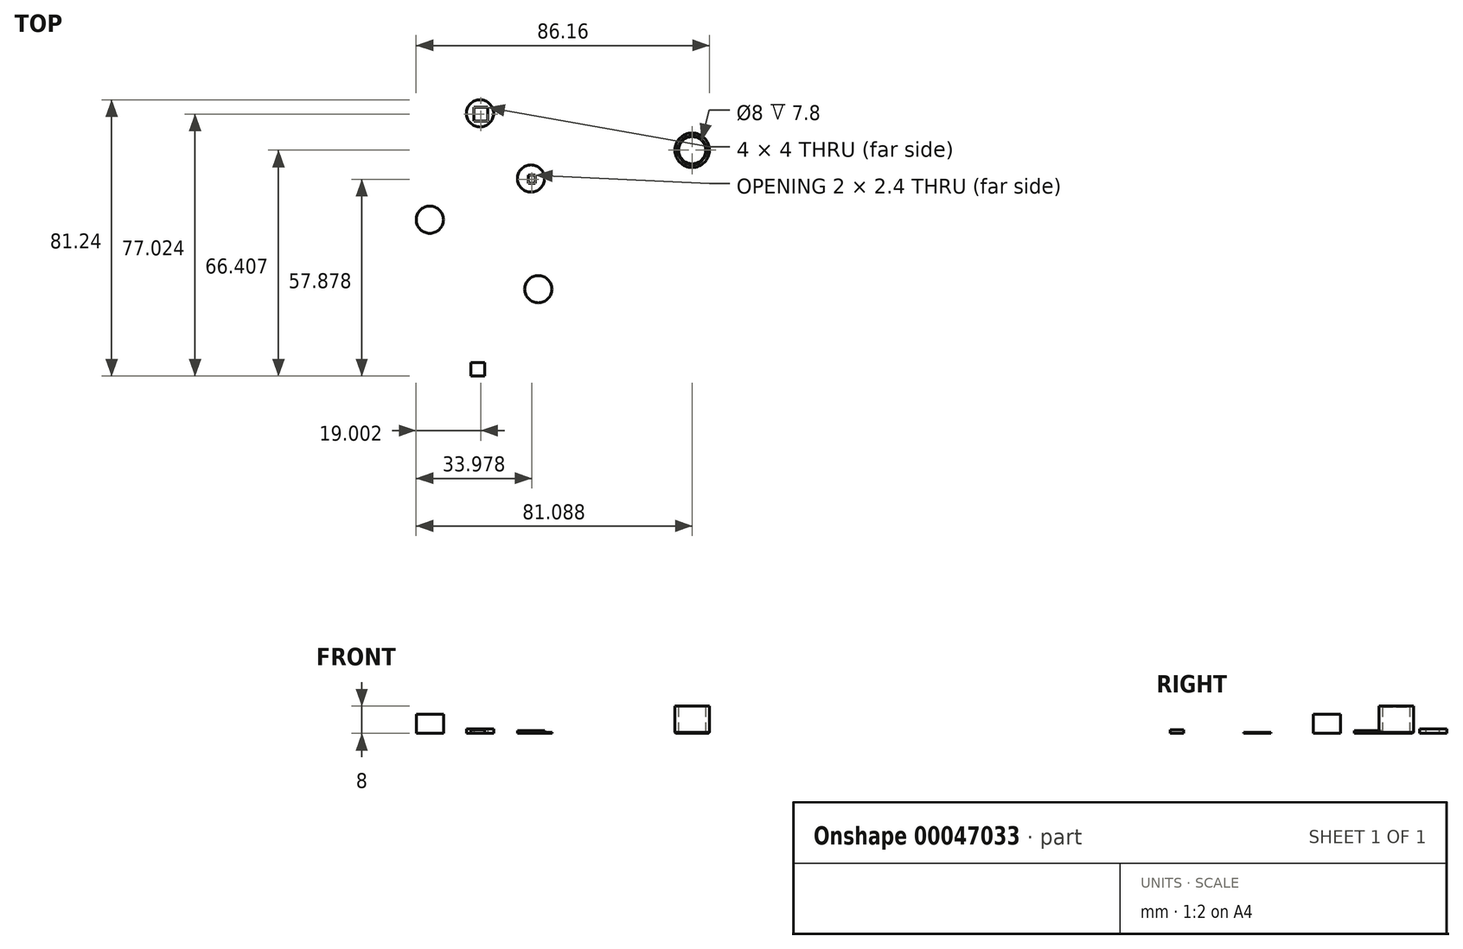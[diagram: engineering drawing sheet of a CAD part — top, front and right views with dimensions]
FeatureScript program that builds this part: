
annotation { "Feature Type Name" : "Feature", "Feature Type Description" : "" }
export const myFeature = defineFeature(function(context is Context, id is Id, definition is map)
    precondition{}
    {
        {
            var Q0;
            Q0=qCreatedBy(makeId("Top.planeOp"),FACE);
            var sketch = newSketch(context, id + "F0", { "sketchPlane" : qUnion([Q0])});
            skLineSegment(sketch, "E0.bottom", {"start": v(-30.94, 27.88) * mm, "end": v(-28.94, 27.88) * mm});
            skLineSegment(sketch, "E0.top", {"start": v(-30.94, 25.48) * mm, "end": v(-28.94, 25.48) * mm});
            skLineSegment(sketch, "E0.left", {"start": v(-30.94, 27.88) * mm, "end": v(-30.94, 25.48) * mm});
            skLineSegment(sketch, "E0.right", {"start": v(-28.94, 27.88) * mm, "end": v(-28.94, 25.48) * mm});
            skLineSegment(sketch, "E1", {"start": v(-28.94, 25.48) * mm, "end": v(-26.99, 25.48) * mm, "construction": true});
            skLineSegment(sketch, "E2", {"start": v(-26.99, 25.48) * mm, "end": v(-26.99, 23.28) * mm, "construction": true});
            skLineSegment(sketch, "E3", {"start": v(-28.94, 27.88) * mm, "end": v(-26.38, 27.88) * mm, "construction": true});
            skLineSegment(sketch, "E4", {"start": v(-26.38, 27.88) * mm, "end": v(-26.38, 29.87) * mm, "construction": true});
            skLineSegment(sketch, "E5", {"start": v(-30.94, 25.48) * mm, "end": v(-32.43, 25.48) * mm, "construction": true});
            skLineSegment(sketch, "E6", {"start": v(-32.43, 25.48) * mm, "end": v(-32.43, 22.62) * mm, "construction": true});
            skCircle(sketch, "E7", {"center": v(-30.19, 26.9) * mm, "radius": 4.83 * mm, "construction": true});
            skCircle(sketch, "E8", {"center": v(-30.19, 26.9) * mm, "radius": 4 * mm});
            skLineSegment(sketch, "E9", {"start": v(-30.56, 27.5) * mm, "end": v(-31.15, 27.5) * mm});
            skLineSegment(sketch, "E10", {"start": v(-30.56, 27.37) * mm, "end": v(-30.56, 28.22) * mm});
            skArc(sketch, "E11", {"start": v(-30.56, 27.88) * mm, "mid": v(-30.83, 27.77) * mm, "end": v(-30.94, 27.5) * mm});
            skSolve(sketch);
        }
        {
            var Q0;
            Q0=makeQuery(id+"F0.imprint","IMPRINT",FACE,{"disambiguationData":[TD([[makeQuery(id+"F0.imprint","IMPRINT",EDGE,{"derivedFrom":sQuery(id+"F0.wireOp",EDGE,"E8")}),1.0]])]});
            extrude(context, id + "F1", {"entities" : qUnion([Q0]), "depth" : 0.79 * mm});
        }
        {
            var Q0;
            Q0=qCreatedBy(makeId("Top.planeOp"),FACE);
            var sketch = newSketch(context, id + "F2", { "sketchPlane" : qUnion([Q0])});
            skLineSegment(sketch, "E12", {"start": v(-43.92, 44.62) * mm, "end": v(-41.97, 44.62) * mm, "construction": true});
            skLineSegment(sketch, "E13", {"start": v(-41.97, 44.62) * mm, "end": v(-41.97, 42.43) * mm, "construction": true});
            skLineSegment(sketch, "E14", {"start": v(-43.92, 47.02) * mm, "end": v(-41.36, 47.02) * mm, "construction": true});
            skLineSegment(sketch, "E15.right", {"start": v(-43.92, 47.02) * mm, "end": v(-43.92, 44.62) * mm, "construction": true});
            skLineSegment(sketch, "E15.left", {"start": v(-45.92, 47.02) * mm, "end": v(-45.92, 44.62) * mm, "construction": true});
            skLineSegment(sketch, "E16", {"start": v(-41.36, 47.02) * mm, "end": v(-41.36, 49.01) * mm, "construction": true});
            skLineSegment(sketch, "E15.top", {"start": v(-45.92, 44.62) * mm, "end": v(-43.92, 44.62) * mm, "construction": true});
            skLineSegment(sketch, "E17", {"start": v(-45.92, 44.62) * mm, "end": v(-47.4, 44.62) * mm, "construction": true});
            skLineSegment(sketch, "E15.bottom", {"start": v(-45.92, 47.02) * mm, "end": v(-43.92, 47.02) * mm, "construction": true});
            skLineSegment(sketch, "E18", {"start": v(-47.4, 44.62) * mm, "end": v(-47.4, 41.77) * mm, "construction": true});
            skCircle(sketch, "E19", {"center": v(-45.16, 46.04) * mm, "radius": 4.83 * mm, "construction": true});
            skCircle(sketch, "E20", {"center": v(-45.16, 46.04) * mm, "radius": 4 * mm});
            skLineSegment(sketch, "E21", {"start": v(-45.92, 47.02) * mm, "end": v(-46.92, 47.02) * mm, "construction": true});
            skLineSegment(sketch, "E22", {"start": v(-45.92, 47.02) * mm, "end": v(-45.92, 47.82) * mm, "construction": true});
            skLineSegment(sketch, "E23", {"start": v(-43.92, 44.62) * mm, "end": v(-42.92, 44.62) * mm, "construction": true});
            skLineSegment(sketch, "E24", {"start": v(-43.92, 44.62) * mm, "end": v(-43.92, 43.82) * mm, "construction": true});
            skLineSegment(sketch, "E25", {"start": v(-46.92, 47.02) * mm, "end": v(-46.92, 47.82) * mm, "construction": true});
            skLineSegment(sketch, "E26", {"start": v(-46.92, 47.82) * mm, "end": v(-45.92, 47.82) * mm, "construction": true});
            skLineSegment(sketch, "E27", {"start": v(-43.92, 43.82) * mm, "end": v(-42.92, 43.82) * mm, "construction": true});
            skLineSegment(sketch, "E28", {"start": v(-42.92, 43.82) * mm, "end": v(-42.92, 44.62) * mm, "construction": true});
            skLineSegment(sketch, "E29.bottom", {"start": v(-46.92, 47.82) * mm, "end": v(-42.92, 47.82) * mm});
            skLineSegment(sketch, "E29.top", {"start": v(-46.92, 43.82) * mm, "end": v(-42.92, 43.82) * mm});
            skLineSegment(sketch, "E29.left", {"start": v(-46.92, 47.82) * mm, "end": v(-46.92, 43.82) * mm});
            skLineSegment(sketch, "E29.right", {"start": v(-42.92, 47.82) * mm, "end": v(-42.92, 43.82) * mm});
            skSolve(sketch);
        }
        {
            var Q0;
            Q0 = qSketchRegion(id + "F2", true);
            extrude(context, id + "F3", {"entities" : qUnion([Q0]), "depth" : 1.27 * mm});
        }
        {
            var Q0;
            Q0=qCreatedBy(makeId("Top.planeOp"),FACE);
            var sketch = newSketch(context, id + "F4", { "sketchPlane" : qUnion([Q0])});
            skCircle(sketch, "E30", {"center": v(-59.92, 14.77) * mm, "radius": 4 * mm});
            skSolve(sketch);
        }
        {
            var Q0;
            Q0 = qSketchRegion(id + "F4", true);
            extrude(context, id + "F5", {"entities" : qUnion([Q0]), "depth" : 5.6 * mm});
        }
        {
            var Q0;
            Q0=qCreatedBy(makeId("Top.planeOp"),FACE);
            var sketch = newSketch(context, id + "F6", { "sketchPlane" : qUnion([Q0])});
            skCircle(sketch, "E31", {"center": v(17.17, 35.2) * mm, "radius": 5.07 * mm});
            skCircle(sketch, "E32", {"center": v(17.17, 35.2) * mm, "radius": 4 * mm});
            skSolve(sketch);
        }
        {
            var Q0;
            Q0 = qSketchRegion(id + "F6", true);
            extrude(context, id + "F7", {"entities" : qUnion([Q0]), "depth" : 8 * mm});
        }
        {
            var Q0;
            Q0=makeQuery(id+"F7.opExtrude","CAP_EDGE",EDGE,{"disambiguationData":[OSD([sQuery(id+"F6.wireOp",EDGE,"E32")])],"isStart":false});
            chamfer(context, id + "F8", {"entities" : qUnion([Q0]), "width" : 0.2 * mm, "tangentPropagation" : true});
        }
        {
            var Q0;
            Q0=makeQuery(id+"F7.opExtrude","CAP_EDGE",EDGE,{"disambiguationData":[OSD([sQuery(id+"F6.wireOp",EDGE,"E31")])],"isStart":true});
            chamfer(context, id + "F9", {"entities" : qUnion([Q0]), "width" : 0.3 * mm, "tangentPropagation" : true});
        }
        {
            var Q0;
            Q0=qCreatedBy(makeId("Top.planeOp"),FACE);
            var sketch = newSketch(context, id + "F10", { "sketchPlane" : qUnion([Q0])});
            skCircle(sketch, "E33", {"center": v(-28.04, -5.64) * mm, "radius": 4 * mm});
            skSolve(sketch);
        }
        {
            var Q0;
            Q0 = qSketchRegion(id + "F10", true);
            extrude(context, id + "F11", {"entities" : qUnion([Q0]), "depth" : 0.25 * mm});
        }
        {
            var Q0;
            Q0=qCreatedBy(makeId("Top.planeOp"),FACE);
            var sketch = newSketch(context, id + "F12", { "sketchPlane" : qUnion([Q0])});
            skLineSegment(sketch, "E34.bottom", {"start": v(-47.81, -27.21) * mm, "end": v(-43.82, -27.21) * mm});
            skLineSegment(sketch, "E34.top", {"start": v(-47.81, -31.2) * mm, "end": v(-43.82, -31.2) * mm});
            skLineSegment(sketch, "E34.left", {"start": v(-47.81, -27.21) * mm, "end": v(-47.81, -31.2) * mm});
            skLineSegment(sketch, "E34.right", {"start": v(-43.82, -27.21) * mm, "end": v(-43.82, -31.2) * mm});
            skSolve(sketch);
        }
        {
            var Q0;
            Q0=makeQuery(id+"F12.imprint","IMPRINT",FACE,{"disambiguationData":[TD([[makeQuery(id+"F12.imprint","IMPRINT",EDGE,{"derivedFrom":sQuery(id+"F12.wireOp",EDGE,"E34.bottom")}),-1.0]])]});
            extrude(context, id + "F13", {"entities" : qUnion([Q0]), "depth" : 1.1 * mm});
        }
    });
